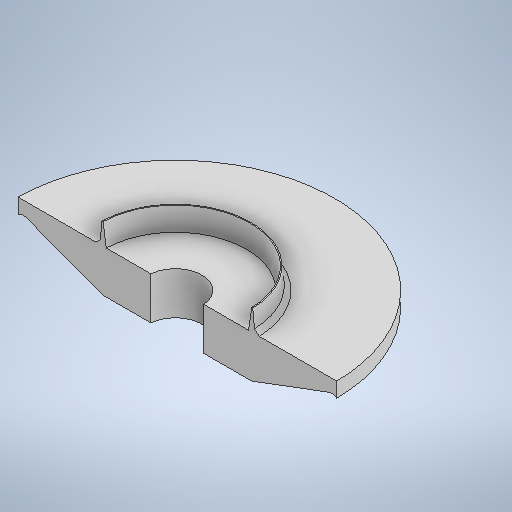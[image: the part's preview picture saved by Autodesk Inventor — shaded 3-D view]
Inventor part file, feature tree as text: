
AUTODESK INVENTOR PART (.ipt)
format: ipt  version: 2025 (Build 290162000, 162)  size: 280,576 bytes
history: native  units: mm
features: sketch x4, chamfer x2, other x1, revolve x1, fillet x1, extrude x1
ambient origin geometry x8: Origin, YZ Plane, XZ Plane, XY Plane, X Axis, Y Axis, Z Axis, Center Point
bodies: Solid1 (feature_tree), Body (feature_tree)
feature tree (10):
  chamfer  "Bottom Chamfer"  Distance=2.0mm
  other  "Centering Lip"
  revolve  "Revolution2"  [1 undecoded]
  fillet  "Fillet1"  Radius=0.3mm
  extrude  "Extrusion5"  TaperAngle=90.0deg  [1 undecoded]
  chamfer  "Chamfer3"  Distance=0.3mm
  sketch  "Sketch1"  dims[d0=2.5mm]
  sketch  "Sketch4"  dims[d1=15.0mm d2=2.0mm d3=0.0mm]
  sketch  "Sketch6"  dims[d11=1.5mm d12=4.0mm d13=45.0deg d16=1.0mm d17=0.3mm]
  sketch  "Sketch7"  dims[d18=3.65mm d21=90.0deg d27=0.3mm d28=0.7mm d29=90.0deg d30=0.3mm d31=0.1mm d32=10.0mm d33=0.0mm d34=0.1mm d35=0.2mm d36=2.0mm d37=45.0deg]
note: 2 required parameter values undecoded (feature->parameter linkage not recoverable at this tier; creation-order binding heuristic only, values carry confidence <= 0.55)